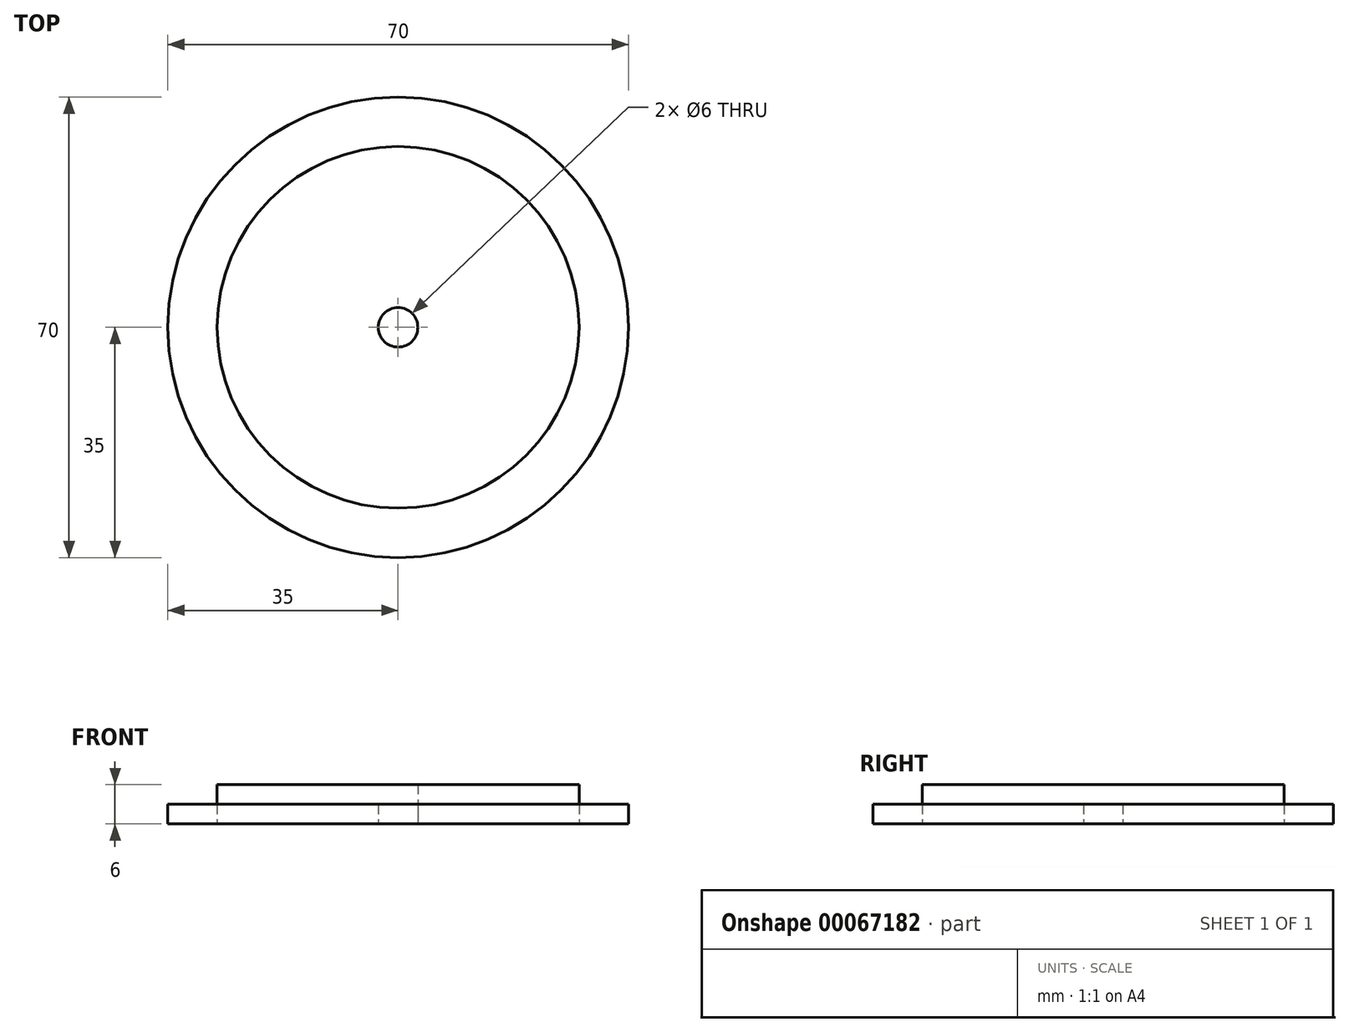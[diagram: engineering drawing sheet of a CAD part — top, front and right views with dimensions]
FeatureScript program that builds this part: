
annotation { "Feature Type Name" : "Feature", "Feature Type Description" : "" }
export const myFeature = defineFeature(function(context is Context, id is Id, definition is map)
    precondition{}
    {
        {
            var Q0;
            Q0=qCreatedBy(makeId("Top.planeOp"),FACE);
            var sketch = newSketch(context, id + "F0", { "sketchPlane" : qUnion([Q0])});
            skCircle(sketch, "E0", {"center": v(0, 0) * mm, "radius": 35 * mm});
            skCircle(sketch, "E1", {"center": v(0, 0) * mm, "radius": 27.5 * mm});
            skCircle(sketch, "E2", {"center": v(0, 0) * mm, "radius": 3 * mm});
            skSolve(sketch);
        }
        {
            var Q0;
            Q0=makeQuery(id+"F0.imprint","IMPRINT",FACE,{"disambiguationData":[TD([[makeQuery(id+"F0.imprint","IMPRINT",EDGE,{"derivedFrom":sQuery(id+"F0.wireOp",EDGE,"E0")}),1.0]])]});
            var Q1;
            Q1=makeQuery(id+"F0.imprint","IMPRINT",FACE,{"disambiguationData":[TD([[makeQuery(id+"F0.imprint","IMPRINT",EDGE,{"derivedFrom":sQuery(id+"F0.wireOp",EDGE,"E1")}),1.0]])]});
            extrude(context, id + "F1", {"entities" : qUnion([Q0, Q1]), "depth" : 3 * mm});
        }
        {
            var Q0;
            Q0=makeQuery(id+"F0.imprint","IMPRINT",FACE,{"disambiguationData":[TD([[makeQuery(id+"F0.imprint","IMPRINT",EDGE,{"derivedFrom":sQuery(id+"F0.wireOp",EDGE,"E1")}),1.0]])]});
            extrude(context, id + "F2", {"entities" : qUnion([Q0]), "depth" : 6 * mm});
        }
    });
